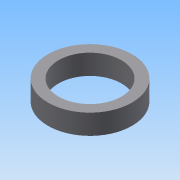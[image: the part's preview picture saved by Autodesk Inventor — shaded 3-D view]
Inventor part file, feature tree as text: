
AUTODESK INVENTOR PART (.ipt)
format: ipt  version: 2015 (Build 190159000, 159)  size: 92,160 bytes
history: native  units: mm
features: extrude x1, sketch x1
ambient origin geometry x8: Origin, YZ Plane, XZ Plane, XY Plane, X Axis, Y Axis, Z Axis, Center Point
bodies: 实体1 (feature_tree)
feature tree (2):
  extrude  "拉伸1"  Depth=9.581mm
  sketch  "草图1"  dims[d0=40.0mm d1=30.0mm d2=9.581mm d3=0.0mm]
